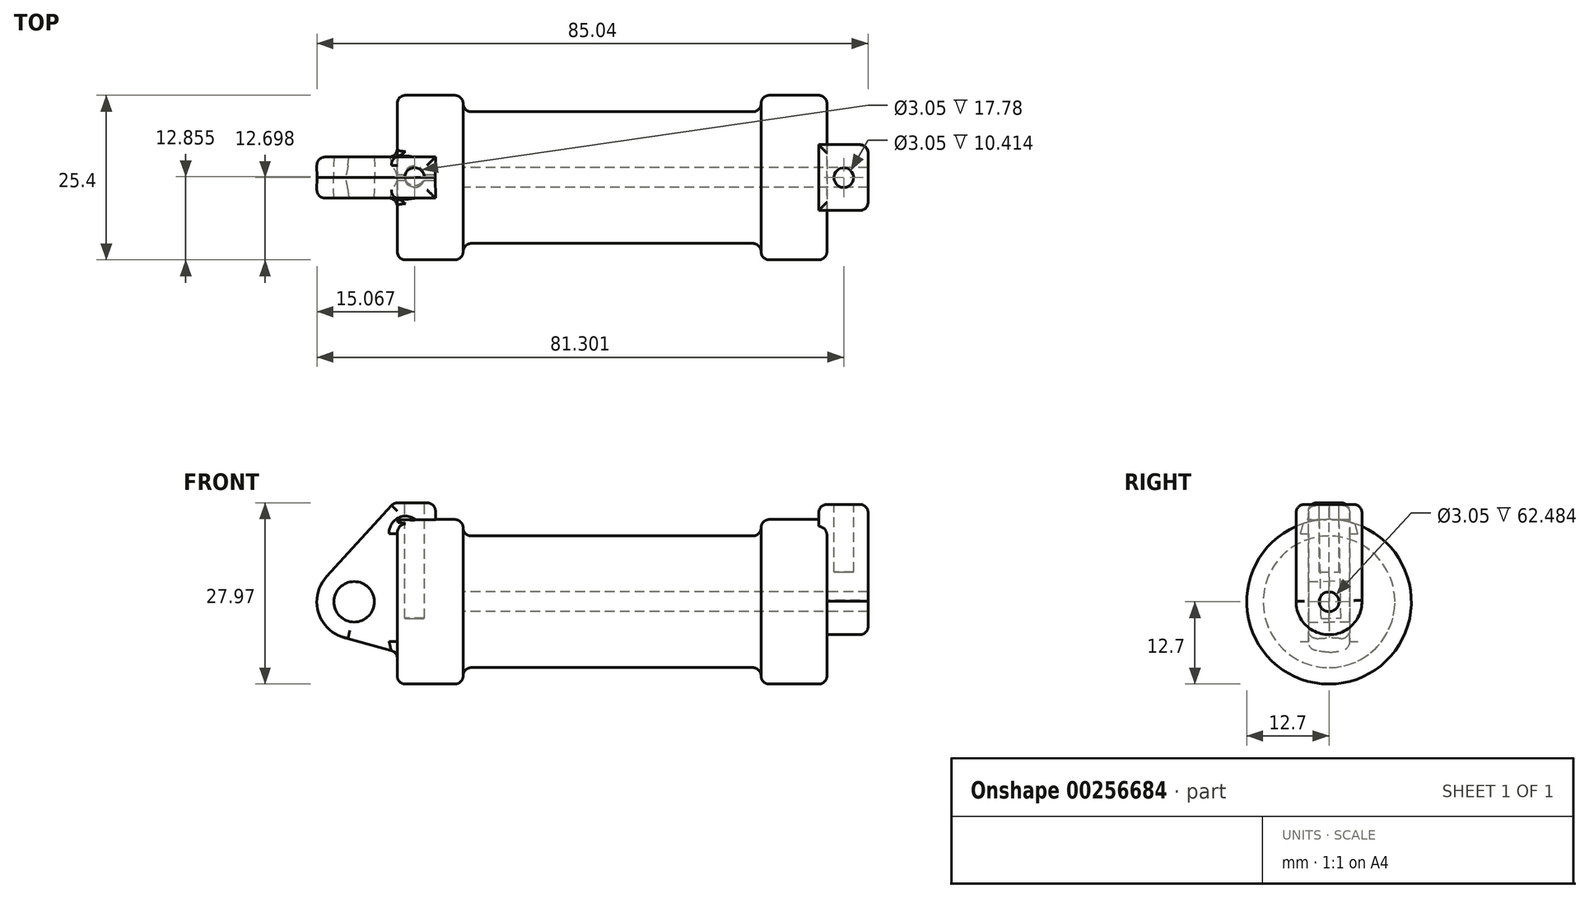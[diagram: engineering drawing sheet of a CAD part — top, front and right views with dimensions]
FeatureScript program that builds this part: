
annotation { "Feature Type Name" : "Feature", "Feature Type Description" : "" }
export const myFeature = defineFeature(function(context is Context, id is Id, definition is map)
    precondition{}
    {
        {
            var Q0;
            Q0=qCreatedBy(makeId("Front.planeOp"),FACE);
            var sketch = newSketch(context, id + "F0", { "sketchPlane" : qUnion([Q0])});
            skLineSegment(sketch, "E0", {"start": v(0, 0) * mm, "end": v(0, 12.7) * mm});
            skLineSegment(sketch, "E1", {"start": v(0, 12.7) * mm, "end": v(10.16, 12.7) * mm});
            skLineSegment(sketch, "E2", {"start": v(10.16, 12.7) * mm, "end": v(10.16, 10.16) * mm});
            skLineSegment(sketch, "E3", {"start": v(10.16, 10.16) * mm, "end": v(56.13, 10.16) * mm});
            skLineSegment(sketch, "E4", {"start": v(56.13, 10.16) * mm, "end": v(56.13, 12.7) * mm});
            skLineSegment(sketch, "E5", {"start": v(56.13, 12.7) * mm, "end": v(66.3, 12.7) * mm});
            skLineSegment(sketch, "E6", {"start": v(66.3, 12.7) * mm, "end": v(66.3, 0) * mm});
            skLineSegment(sketch, "E7", {"start": v(66.3, 0) * mm, "end": v(0, 0) * mm});
            skLineSegment(sketch, "E8", {"start": v(5.84, 15.24) * mm, "end": v(-0.5, 15.24) * mm});
            skLineSegment(sketch, "E9", {"start": v(-0.5, 15.24) * mm, "end": v(-10.88, 3.85) * mm});
            skLineSegment(sketch, "E10", {"start": v(0, 0) * mm, "end": v(-6.65, 0) * mm});
            skCircle(sketch, "E11", {"center": v(-6.65, 0) * mm, "radius": 5.72 * mm});
            skCircle(sketch, "E12", {"center": v(-6.65, 0) * mm, "radius": 3.18 * mm});
            skLineSegment(sketch, "E13", {"start": v(5.84, 15.24) * mm, "end": v(5.84, -9.4) * mm});
            skLineSegment(sketch, "E14", {"start": v(5.84, -9.4) * mm, "end": v(-8.18, -5.5) * mm});
            skSolve(sketch);
        }
        {
            var Q0;
            {var subQ0=sQuery(id+"F0.wireOp",EDGE,"E2");Q0=makeQuery(id+"F0.imprint","IMPRINT",FACE,{"disambiguationData":[TD([[makeQuery(id+"F0.imprint","IMPRINT",EDGE,{"derivedFrom":subQ0}),-1.0]])]});}
            var Q1;
            {var subQ0=sQuery(id+"F0.wireOp",EDGE,"E0");Q1=makeQuery(id+"F0.imprint","IMPRINT",FACE,{"disambiguationData":[TD([[makeQuery(id+"F0.imprint","IMPRINT",EDGE,{"derivedFrom":subQ0}),-1.0]])]});}
            var Q2;
            Q2=sQuery(id+"F0.wireOp",EDGE,"E7");
            revolve(context, id + "F1", {"entities" : qUnion([Q0, Q1]), "axis" : qUnion([Q2]), "revolveType" : RevolveType.FULL});
        }
        {
            var Q0;
            {var subQ4=sQuery(id+"F0.wireOp",EDGE,"E12");Q0=makeQuery(id+"F0.imprint","IMPRINT",FACE,{"disambiguationData":[TD([[makeQuery(id+"F0.imprint","IMPRINT",EDGE,{"derivedFrom":subQ4}),-1.0]])]});}
            var Q1;
            {var subQ3=sQuery(id+"F0.wireOp",EDGE,"E0");Q1=makeQuery(id+"F0.imprint","IMPRINT",FACE,{"disambiguationData":[TD([[makeQuery(id+"F0.imprint","IMPRINT",EDGE,{"derivedFrom":subQ3}),1.0]])]});}
            extrude(context, id + "F2", {"entities" : qUnion([Q0, Q1]), "operationType" : NewBodyOperationType.ADD, "depth" : 6.35 * mm, "hasDraft" : true, "draftAngle" : 1 * degree, "symmetric" : true});
        }
        {
            var Q0;
            {var subQ0=sQuery(id+"F0.wireOp",EDGE,"E14");Q0=makeQuery(id+"F0.imprint","IMPRINT",FACE,{"disambiguationData":[TD([[makeQuery(id+"F0.imprint","IMPRINT",EDGE,{"derivedFrom":subQ0}),-1.0]])]});}
            extrude(context, id + "F3", {"entities" : qUnion([Q0]), "operationType" : NewBodyOperationType.ADD, "depth" : 6.35 * mm, "symmetric" : true});
        }
        {
            var Q0;
            Q0=makeQuery(id+"F1.opRevolve","SWEPT_FACE",FACE,{"disambiguationData":[OSD([sQuery(id+"F0.wireOp",EDGE,"E6")])]});
            var sketch = newSketch(context, id + "F4", { "sketchPlane" : qUnion([Q0])});
            skCircle(sketch, "E15", {"center": v(0, 0) * mm, "radius": 5.08 * mm});
            skCircle(sketch, "E16", {"center": v(0, 0) * mm, "radius": 1.52 * mm});
            skLineSegment(sketch, "E17", {"start": v(-5.08, -0.07) * mm, "end": v(-5.08, 15.03) * mm});
            skLineSegment(sketch, "E18", {"start": v(5.08, -0.21) * mm, "end": v(5.08, 15.03) * mm});
            skLineSegment(sketch, "E19", {"start": v(-5.08, 15.03) * mm, "end": v(5.08, 15.03) * mm});
            skSolve(sketch);
        }
        {
            var Q0;
            Q0 = qSketchRegion(id + "F4", true);
            extrude(context, id + "F5", {"entities" : qUnion([Q0]), "operationType" : NewBodyOperationType.ADD, "depth" : 6.35 * mm});
        }
        {
            var Q0;
            Q0 = qSketchRegion(id + "F4", true);
            extrude(context, id + "F6", {"entities" : qUnion([Q0]), "operationType" : NewBodyOperationType.ADD, "oppositeDirection" : true, "depth" : 1.27 * mm});
        }
        {
            var Q0;
            Q0=makeQuery(id+"F5.boolean.opBoolean","SPLIT",FACE,{"disambiguationData":[TD([makeQuery(id+"F5.opExtrude","SWEPT_FACE",FACE,{"disambiguationData":[OSD([sQuery(id+"F4.wireOp",EDGE,"E16")])]})])],"derivedFrom":makeQuery(id+"F1.opRevolve","SWEPT_FACE",FACE,{"disambiguationData":[OSD([sQuery(id+"F0.wireOp",EDGE,"E6")])]})});
            var Q1;
            Q1=makeQuery(id+"F1.opRevolve","SWEPT_FACE",FACE,{"disambiguationData":[OSD([sQuery(id+"F0.wireOp",EDGE,"E2")])]});
            extrude(context, id + "F7", {"entities" : qUnion([Q0]), "operationType" : NewBodyOperationType.REMOVE, "endBound" : BoundingType.UP_TO_SURFACE, "oppositeDirection" : true, "endBoundEntityFace" : qUnion([Q1]), "depth" : 25.4 * mm});
        }
        {
            var Q0;
            {var subQ0=sQuery(id+"F4.wireOp",EDGE,"E19");Q0=makeQuery(id+"F6.boolean.opBoolean","MERGE",FACE,{"derivedFrom":[makeQuery(id+"F5.opExtrude","SWEPT_FACE",FACE,{"disambiguationData":[OSD([subQ0])]}),makeQuery(id+"F6.opExtrude","SWEPT_FACE",FACE,{"disambiguationData":[OSD([subQ0])]})]});}
            var sketch = newSketch(context, id + "F8", { "sketchPlane" : qUnion([Q0])});
            skCircle(sketch, "E20", {"center": v(68.9, 0) * mm, "radius": 1.52 * mm});
            skPoint(sketch, "E20.centerSnap0", {"position": v(65.02, 0) * mm});
            skSolve(sketch);
        }
        {
            var Q0;
            Q0=makeQuery(id+"F2.*.split.splitOp","SPLIT",FACE,{"derivedFrom":makeQuery(id+"F2.opExtrude","SWEPT_FACE",FACE,{"disambiguationData":[OSD([sQuery(id+"F0.wireOp",EDGE,"E8")])]}),"isFromBackBody":true});
            var sketch = newSketch(context, id + "F9", { "sketchPlane" : qUnion([Q0])});
            skCircle(sketch, "E21", {"center": v(2.67, 0.27) * mm, "radius": 1.52 * mm});
            skSolve(sketch);
        }
        {
            var Q0;
            {var subQ0=sQuery(id+"F9.wireOp",EDGE,"E21");var subQ1=makeQuery(id+"F2.opExtrude","SWEPT_FACE",FACE,{"disambiguationData":[OSD([sQuery(id+"F0.wireOp",EDGE,"E8")])]});var subQ2=makeQuery(id+"F2.*.booleanUnion.opBoolean","MERGE",EDGE,{"derivedFrom":[makeQuery(id+"F2.*.split.splitOp","SPLIT_SURFACE_INTERSECT",EDGE,{"derivedFrom":[subQ1]}),makeQuery(id+"F2.*.split.splitOp","SPLIT_SURFACE_INTERSECT",EDGE,{"derivedFrom":[subQ1],"isFromBackBody":true})]});var subQ3=makeQuery(id+"F9.imprint","INTERSECT",VERTEX,{"disambiguationData":[OD(0.0)],"derivedFrom":[subQ2,subQ0]});Q0=makeQuery(id+"F9.imprint","IMPRINT",FACE,{"disambiguationData":[TD([[makeQuery(id+"F9.imprint","IMPRINT",EDGE,{"disambiguationData":[TD([[subQ3,-1.0]])],"derivedFrom":subQ0}),1.0]])]});}
            var Q1;
            {var subQ0=sQuery(id+"F9.wireOp",EDGE,"E21");var subQ1=makeQuery(id+"F2.opExtrude","SWEPT_FACE",FACE,{"disambiguationData":[OSD([sQuery(id+"F0.wireOp",EDGE,"E8")])]});var subQ2=makeQuery(id+"F2.*.booleanUnion.opBoolean","MERGE",EDGE,{"derivedFrom":[makeQuery(id+"F2.*.split.splitOp","SPLIT_SURFACE_INTERSECT",EDGE,{"derivedFrom":[subQ1]}),makeQuery(id+"F2.*.split.splitOp","SPLIT_SURFACE_INTERSECT",EDGE,{"derivedFrom":[subQ1],"isFromBackBody":true})]});var subQ3=makeQuery(id+"F9.imprint","INTERSECT",VERTEX,{"disambiguationData":[OD(0.0)],"derivedFrom":[subQ2,subQ0]});Q1=makeQuery(id+"F9.imprint","IMPRINT",FACE,{"disambiguationData":[TD([[makeQuery(id+"F9.imprint","IMPRINT",EDGE,{"disambiguationData":[TD([[subQ3,1.0]])],"derivedFrom":subQ0}),1.0]])]});}
            extrude(context, id + "F10", {"entities" : qUnion([Q0, Q1]), "operationType" : NewBodyOperationType.REMOVE, "oppositeDirection" : true, "depth" : 17.78 * mm});
        }
        {
            var Q0;
            Q0=makeQuery(id+"F8.imprint","IMPRINT",FACE,{"disambiguationData":[TD([[makeQuery(id+"F8.imprint","IMPRINT",EDGE,{"derivedFrom":sQuery(id+"F8.wireOp",EDGE,"E20")}),1.0]])]});
            extrude(context, id + "F11", {"entities" : qUnion([Q0]), "operationType" : NewBodyOperationType.REMOVE, "oppositeDirection" : true, "depth" : 10.4 * mm});
        }
        {
            var Q0;
            Q0=makeQuery(id+"F1.opRevolve","SWEPT_EDGE",EDGE,{"disambiguationData":[OSD([sQuery(id+"F0.wireOp",EDGE,"E2"),sQuery(id+"F0.wireOp",EDGE,"E3")])]});
            var Q1;
            Q1=makeQuery(id+"F1.opRevolve","SWEPT_EDGE",EDGE,{"disambiguationData":[OSD([sQuery(id+"F0.wireOp",EDGE,"E1"),sQuery(id+"F0.wireOp",EDGE,"E2")])]});
            var Q2;
            Q2=makeQuery(id+"F1.opRevolve","SWEPT_EDGE",EDGE,{"disambiguationData":[OSD([sQuery(id+"F0.wireOp",EDGE,"E4"),sQuery(id+"F0.wireOp",EDGE,"E5")])]});
            var Q3;
            Q3=makeQuery(id+"F1.opRevolve","SWEPT_EDGE",EDGE,{"disambiguationData":[OSD([sQuery(id+"F0.wireOp",EDGE,"E3"),sQuery(id+"F0.wireOp",EDGE,"E4")])]});
            var Q4;
            Q4=makeQuery(id+"F1.opRevolve","SWEPT_EDGE",EDGE,{"disambiguationData":[OSD([sQuery(id+"F0.wireOp",EDGE,"E0"),sQuery(id+"F0.wireOp",EDGE,"E1")])]});
            var Q5;
            Q5=makeQuery(id+"F5.boolean.opBoolean","SPLIT",EDGE,{"disambiguationData":[OD(1.0)],"derivedFrom":makeQuery(id+"F1.opRevolve","SWEPT_EDGE",EDGE,{"disambiguationData":[OSD([sQuery(id+"F0.wireOp",EDGE,"E5"),sQuery(id+"F0.wireOp",EDGE,"E6")])]})});
            fillet(context, id + "F12", {"entities" : qUnion([Q0, Q1, Q2, Q3, Q4, Q5]), "radius" : 1.27 * mm, "tangentPropagation" : true, "allowEdgeOverflow" : false});
        }
        {
            var Q0;
            Q0=makeQuery(id+"F5.opExtrude","CAP_EDGE",EDGE,{"disambiguationData":[OSD([sQuery(id+"F4.wireOp",EDGE,"E17")])],"isStart":false});
            var Q1;
            Q1=makeQuery(id+"F5.opExtrude","CAP_EDGE",EDGE,{"disambiguationData":[OSD([sQuery(id+"F4.wireOp",EDGE,"E18")])],"isStart":false});
            var Q2;
            Q2=makeQuery(id+"F5.opExtrude","CAP_EDGE",EDGE,{"disambiguationData":[OSD([sQuery(id+"F4.wireOp",EDGE,"E19")])],"isStart":false});
            var Q3;
            Q3=makeQuery(id+"F5.opExtrude","CAP_EDGE",EDGE,{"disambiguationData":[OSD([sQuery(id+"F4.wireOp",EDGE,"E15")])],"isStart":false});
            var Q4;
            Q4=makeQuery(id+"F5.opExtrude","CAP_EDGE",EDGE,{"disambiguationData":[OSD([sQuery(id+"F4.wireOp",EDGE,"E15")])],"isStart":true});
            var Q5;
            {var subQ0=sQuery(id+"F4.wireOp",EDGE,"E17");var subQ1=sQuery(id+"F4.wireOp",EDGE,"E15");Q5=makeQuery(id+"F5.boolean.opBoolean","SPLIT",EDGE,{"disambiguationData":[TD([makeQuery(id+"F5.opExtrude","SWEPT_FACE",FACE,{"disambiguationData":[OSD([subQ1])]})])],"derivedFrom":makeQuery(id+"F5.opExtrude","CAP_EDGE",EDGE,{"disambiguationData":[OSD([subQ0])],"isStart":true})});}
            var Q6;
            {var subQ0=sQuery(id+"F4.wireOp",EDGE,"E18");var subQ1=sQuery(id+"F4.wireOp",EDGE,"E15");Q6=makeQuery(id+"F5.boolean.opBoolean","SPLIT",EDGE,{"disambiguationData":[TD([makeQuery(id+"F5.opExtrude","SWEPT_FACE",FACE,{"disambiguationData":[OSD([subQ1])]})])],"derivedFrom":makeQuery(id+"F5.opExtrude","CAP_EDGE",EDGE,{"disambiguationData":[OSD([subQ0])],"isStart":true})});}
            fillet(context, id + "F13", {"entities" : qUnion([Q0, Q1, Q2, Q3, Q4, Q5, Q6]), "radius" : 1.27 * mm, "tangentPropagation" : true, "allowEdgeOverflow" : false});
        }
        {
            var Q0;
            {var subQ0=sQuery(id+"F4.wireOp",EDGE,"E19");var subQ1=sQuery(id+"F4.wireOp",EDGE,"E18");Q0=makeQuery(id+"F6.boolean.opBoolean","MERGE",EDGE,{"derivedFrom":[makeQuery(id+"F5.opExtrude","SWEPT_EDGE",EDGE,{"disambiguationData":[OSD([subQ1,subQ0])]}),makeQuery(id+"F6.opExtrude","SWEPT_EDGE",EDGE,{"disambiguationData":[OSD([subQ1,subQ0])]})]});}
            var Q1;
            Q1=makeQuery(id+"F6.opExtrude","CAP_EDGE",EDGE,{"disambiguationData":[OSD([sQuery(id+"F4.wireOp",EDGE,"E19")])],"isStart":false});
            var Q2;
            {var subQ0=sQuery(id+"F4.wireOp",EDGE,"E19");var subQ1=sQuery(id+"F4.wireOp",EDGE,"E17");Q2=makeQuery(id+"F6.boolean.opBoolean","MERGE",EDGE,{"derivedFrom":[makeQuery(id+"F5.opExtrude","SWEPT_EDGE",EDGE,{"disambiguationData":[OSD([subQ1,subQ0])]}),makeQuery(id+"F6.opExtrude","SWEPT_EDGE",EDGE,{"disambiguationData":[OSD([subQ1,subQ0])]})]});}
            fillet(context, id + "F14", {"entities" : qUnion([Q0, Q1, Q2]), "radius" : 1.27 * mm, "tangentPropagation" : true, "allowEdgeOverflow" : false});
        }
        {
            var Q0;
            Q0=makeQuery(id+"F3.opExtrude","CAP_EDGE",EDGE,{"disambiguationData":[OSD([sQuery(id+"F0.wireOp",EDGE,"E14")])],"isStart":false});
            var Q1;
            Q1=makeQuery(id+"F3.boolean.opBoolean","INTERSECT",EDGE,{"derivedFrom":[makeQuery(id+"F1.opRevolve","SWEPT_FACE",FACE,{"disambiguationData":[OSD([sQuery(id+"F0.wireOp",EDGE,"E0")])]}),makeQuery(id+"F3.opExtrude","CAP_FACE",FACE,{"disambiguationData":[OSD([sQuery(id+"F0.wireOp",EDGE,"E7"),sQuery(id+"F0.wireOp",EDGE,"E10"),sQuery(id+"F0.wireOp",EDGE,"E11"),sQuery(id+"F0.wireOp",EDGE,"E13"),sQuery(id+"F0.wireOp",EDGE,"E14")])],"isStart":false})]});
            var Q2;
            Q2=makeQuery(id+"F2.opExtrude","CAP_EDGE",EDGE,{"disambiguationData":[OSD([sQuery(id+"F0.wireOp",EDGE,"E9")])],"isStart":false});
            var Q3;
            Q3=makeQuery(id+"F3.boolean.opBoolean","INTERSECT",EDGE,{"derivedFrom":[makeQuery(id+"F1.opRevolve","SWEPT_FACE",FACE,{"disambiguationData":[OSD([sQuery(id+"F0.wireOp",EDGE,"E0")])]}),makeQuery(id+"F3.opExtrude","CAP_FACE",FACE,{"disambiguationData":[OSD([sQuery(id+"F0.wireOp",EDGE,"E7"),sQuery(id+"F0.wireOp",EDGE,"E10"),sQuery(id+"F0.wireOp",EDGE,"E11"),sQuery(id+"F0.wireOp",EDGE,"E13"),sQuery(id+"F0.wireOp",EDGE,"E14")])],"isStart":true})]});
            var Q4;
            Q4=makeQuery(id+"F3.opExtrude","CAP_EDGE",EDGE,{"disambiguationData":[OSD([sQuery(id+"F0.wireOp",EDGE,"E14")])],"isStart":true});
            var Q5;
            Q5=makeQuery(id+"F2.opExtrude","CAP_EDGE",EDGE,{"disambiguationData":[OSD([sQuery(id+"F0.wireOp",EDGE,"E9")])],"isStart":true});
            fillet(context, id + "F15", {"entities" : qUnion([Q0, Q1, Q2, Q3, Q4, Q5]), "radius" : 1.27 * mm, "tangentPropagation" : true, "allowEdgeOverflow" : false});
        }
        {
            var Q0;
            Q0=makeQuery(id+"F2.opExtrude","CAP_EDGE",EDGE,{"disambiguationData":[OSD([sQuery(id+"F0.wireOp",EDGE,"E8")])],"isStart":false});
            var Q1;
            Q1=makeQuery(id+"F2.opExtrude","CAP_EDGE",EDGE,{"disambiguationData":[OSD([sQuery(id+"F0.wireOp",EDGE,"E8")])],"isStart":true});
            var Q2;
            Q2=makeQuery(id+"F2.*.split.splitOp","SPLIT",EDGE,{"derivedFrom":makeQuery(id+"F2.opExtrude","SWEPT_EDGE",EDGE,{"disambiguationData":[OSD([sQuery(id+"F0.wireOp",EDGE,"E8"),sQuery(id+"F0.wireOp",EDGE,"E13")])]}),"isFromBackBody":true});
            var Q3;
            Q3=makeQuery(id+"F2.*.split.splitOp","SPLIT",EDGE,{"derivedFrom":makeQuery(id+"F2.opExtrude","SWEPT_EDGE",EDGE,{"disambiguationData":[OSD([sQuery(id+"F0.wireOp",EDGE,"E8"),sQuery(id+"F0.wireOp",EDGE,"E13")])]})});
            fillet(context, id + "F16", {"entities" : qUnion([Q0, Q1, Q2, Q3]), "radius" : 1.27 * mm, "tangentPropagation" : true, "allowEdgeOverflow" : false});
        }
    });
